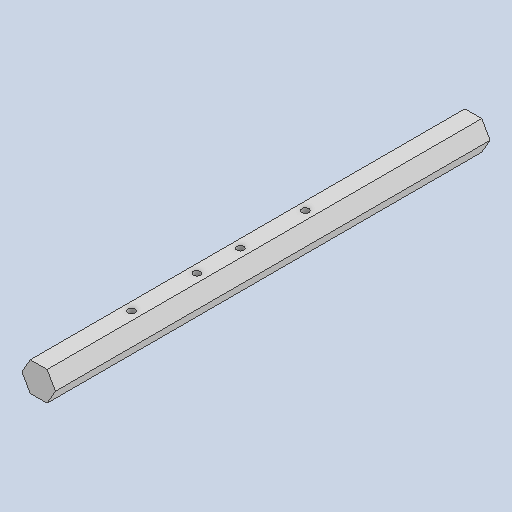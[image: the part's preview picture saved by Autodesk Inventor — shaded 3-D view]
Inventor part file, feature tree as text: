
AUTODESK INVENTOR PART (.ipt)
format: ipt  version: 2022 (Build 260153000, 153)  size: 123,904 bytes
history: native  units: mm
features: extrude x2, sketch x2
ambient origin geometry x8: Origin, YZ Plane, XZ Plane, XY Plane, X Axis, Y Axis, Z Axis, Center Point
bodies: Body1 (feature_tree)
feature tree (4):
  extrude  "Extrusion5"  Depth=3.1mm TaperAngle=360.0deg
  extrude  "Extrusion6"  Depth=80.0mm
  sketch  "Sketch5"  dims[d9=3.1mm d10=60.0mm d12=360.0deg]
  sketch  "Sketch6"  dims[d14=80.0mm d15=0.0mm d16=1.3mm d17=49.1mm d18=37.1mm d19=29.1mm d20=17.1mm d21=6.0mm d22=0.0mm]
